# Revit family: Plumbing-Flushometer-Sloan-Valve-TRF-8196_
name_source: partatom
category: Plumbing Fixtures
units: mm (PartAtom-declared; Revit-internal decimal feet)

## family parameters
Cut with Voids When Loaded = Yes
Host = Face
OmniClass Number = 23.45.05.14.99
OmniClass Title = Other Sanitary Washing Plumbing Fixtures
Part Type = Normal
Room Calculation Point = No
Round Connector Dimension = Use Diameter
Shared = No

## types (5) — shared parameters
Assembly Code = D2020300
CW Connection = Yes
Default Elevation = 0"
Edition number = 1
HW Connection = No
Height = 6 1/4"
Keynote = 15410
Manufacturer = Sloan Valve
Operating Water Pressure = 15 – 80 PSI (103 – 552 kPa)
Product data url = https://bimobject.com
URL = www.sloanvalve.com
Valve Pressure Drop = 0.00 psi
Vent Connection = No
Waste Connection = No
Water Inlet Connection Diameter = 2"
Water Outlet Connection Diameter = 2"
zero-valued in all types: CWFU, HWFU, WFU

## per-type parameters (varying)
| type | Description | Flush Rate | Part Number | Product Material |
| TRF 8196-0.125-OR | 0.125 gpf, Filtered, Polished Chrome Finish, Fixture Connection Rear Spud, Single Flush, Electrical Override, Battery, TruFlush Concealed Sensor Urinal Flushometer. | 0.125 gpf (0.5 Lpf) | 3400104 | Sloan Valve - Finish - Polished Chrome |
| TRF 8196-0.25-SF-OR | 0.25 gpf, Filtered, Brushed Stainless Finish, Fixture Connection Rear Spud, Single Flush, Electrical Override, Battery, TruFlush Concealed Sensor Urinal Flushometer. | 0.25 gpf (0.9 Lpf) | 3400118 | Sloan Valve - Finish - Brushed Stainless Steel |
| TRF 8196-0.5-SF-OR | 0.5 gpf, Filtered, Brushed Stainless Finish, Fixture Connection Rear Spud, Single Flush, Electrical Override, Battery, TruFlush Concealed Sensor Urinal Flushometer. | 0.5 gpf (1.9 Lpf) | 3400117 | Sloan Valve - Finish - Brushed Stainless Steel |
| TRF 8196-0.25-OR | 0.25 gpf, Filtered, Polished Chrome Finish, Fixture Connection Rear Spud, Single Flush, Electrical Override, Battery, TruFlush Concealed Sensor Urinal Flushometer. | 0.25 gpf (0.9 Lpf) | 3400103 | Sloan Valve - Finish - Polished Chrome |
| TRF 8196-0.5-OR | 0.5 gpf, Filtered, Polished Chrome Finish, Fixture Connection Rear Spud, Single Flush, Electrical Override, Battery, TruFlush Concealed Sensor Urinal Flushometer. | 0.5 gpf (1.9 Lpf) | 3400102 | Sloan Valve - Finish - Polished Chrome |

note: column(s) folded — value = type name in every type: Model

## geometry (parser evidence)
native form markers: Sweep x5
no freeform markers — native parametric forms only
